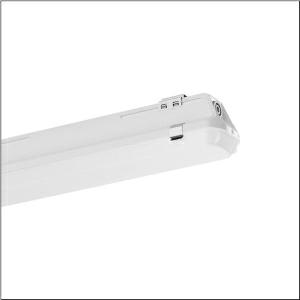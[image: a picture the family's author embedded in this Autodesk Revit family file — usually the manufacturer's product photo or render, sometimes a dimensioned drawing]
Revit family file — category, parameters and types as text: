
# Revit family: monsun_r__21_51fb207p460b005_f6e2
name_source: partatom
category: Lighting Fixtures
units: mm (PartAtom-declared; Revit-internal decimal feet)

## family parameters
Cut with Voids When Loaded = No
Host = Face
Light Source = No
Part Type = Normal
Room Calculation Point = No
Round Connector Dimension = Use Diameter
Shared = No

## types (1)
- Monsun® 21 (1 x LED, 5400 lm, 38 W, 4000K)
    Apparent Load = 38 VA
    CIE Flux Codes = 45 75 93 94 100
    Color Rendering = 80
    Color Temperature = 4000K
    Default Elevation = 1800 mm
    Description = Monsun® 21, damp-proof luminaire, chain hanger, primary optical cover: enclosure, of PC, light emission: direct distribution, primary light characteristic: symmetric, installation type: suspended mounting, surface-mounted, horizontal mounting, vertical mounting, LED, rated luminous flux: 5.400lm, luminous efficacy: 142lm/W, light colour: 840, colour temperature: 4000K, control gear: ECG, with terminal, 3-pole, max. 2.5mm², through-wiring: 5x 2.5mm², mains connection: 220..240V, AC, 50/60Hz, rated input power: 38W, housing, of glass-fibre reinforced polyester, uncoated, bright grey, incl. chain hanger, length: 1.590mm, width: 90mm, height: 88mm, clip for enclosure, of stainless steel (V2A), ceiling mounting element, of stainless steel (V2A), chain hanger, of stainless steel (V2A), protection rating (complete): IP66, insulation class (complete): insulation class I (protective earthing), certification: CE, ENEC, VDE, UKCA, protection symbol: D, impact resistance: IK08, permissible operating ambient temperature: -25..+35°C, standard: EN 50419, EN 60598-2-1, corresponds to IFS (International Featured Standards) requirements for safety and quality in the food industry, for indoor or canopied outdoor use, no direct snow, no direct sun, no direct rain, contact your sales advisor before using the luminaires in applications with unclear chemical exposure, large temperature fluctuations or condensation-forming humidity, LABS conformity tested according to VDMA 24364:2018-05, packaging unit: 1 piece
    Height = 89 mm
    Lamp = 1 x LED
    Lamp Light Flux = 5400 lm
    Lamp Power = 38 W
    Lamp count = 1
    Length = 1590 mm
    Luminous efficacy = 142 lm/W
    Manufacturer = Siteco
    ModVariant = No
    Model = 51FB207P460B005
    Mounting Place = Ceiling
    Mounting Type = Surface mounted
    Number of Poles = 1
    OnlyDefault = Yes
    Power Factor = 1
    Product Name = Monsun® 21
    Product group = damp-proof luminaire
    ProductGroupID = 300
    Protection Class = Protection class I
    Protection Degree = IP 66
    RLX_Detail_Level = 1
    RLX_Emergency_Light_Flux = 0 lm
    RLX_Emergency_Type = 0
    RLX_Emergency_Type_DB = No
    RlxData = <blob elided: 88601 chars, md5=201d997e>
    Socket = socket
    Standby Power = 0 W
    System Light Flux = 5400 lm
    System Power = 38 W
    Type Comments = Product without accessories
    Type Image = l_1319656.jpg
    URL = http://relux.com
    VarID = ---
    Voltage = 0 V
    Weight = 0.00 kg
    Width = 90 mm

## geometry (parser evidence)
native form markers: Blend x4, Sweep x13
no freeform markers — native parametric forms only
